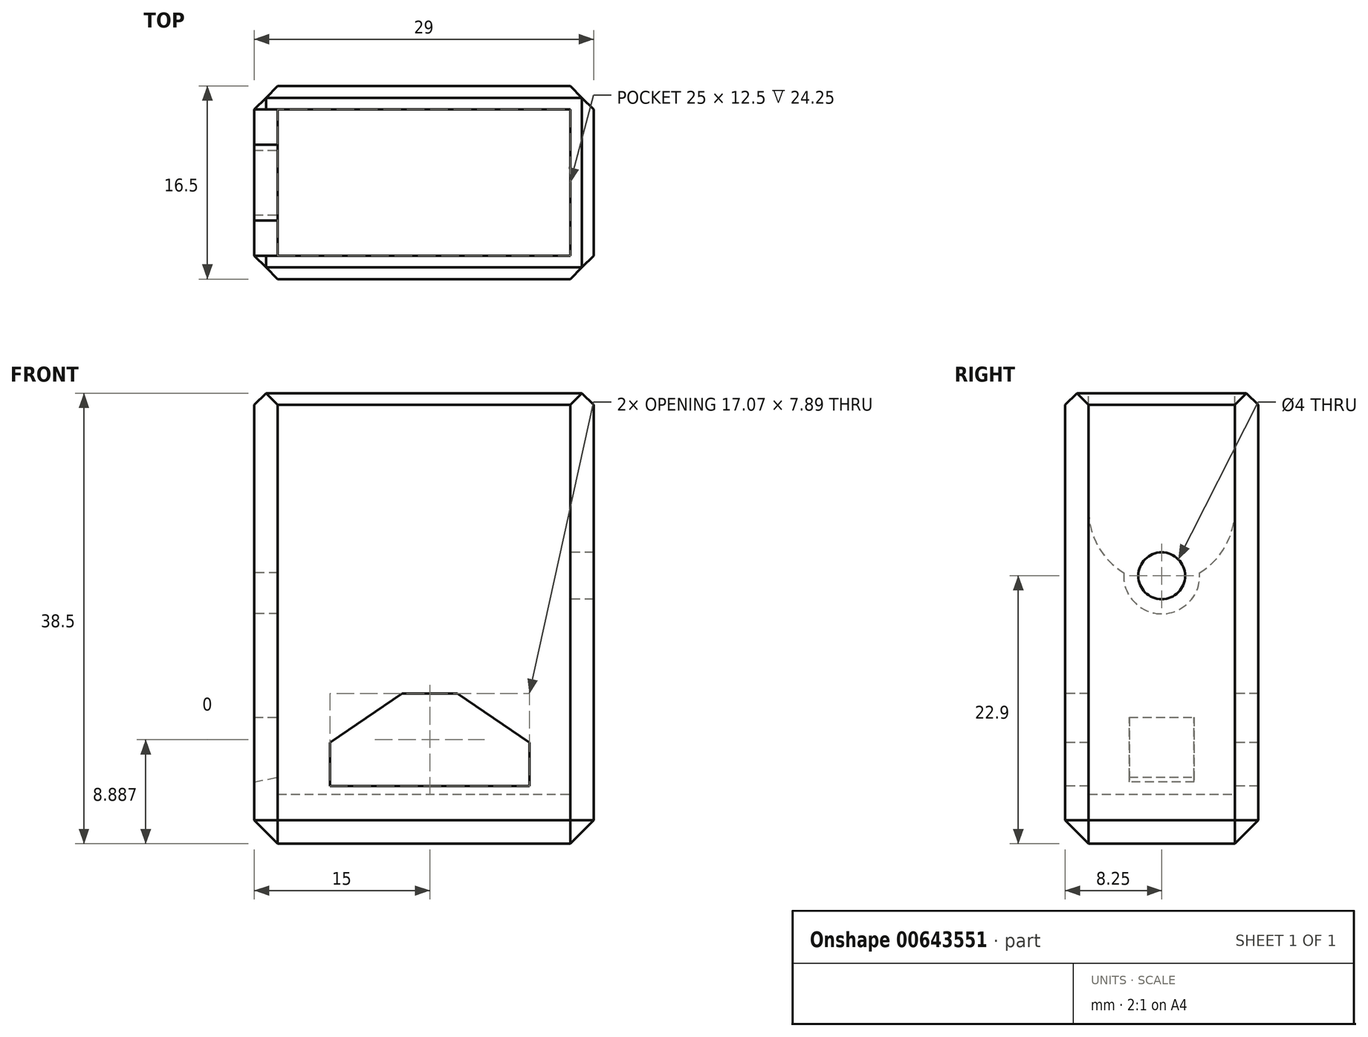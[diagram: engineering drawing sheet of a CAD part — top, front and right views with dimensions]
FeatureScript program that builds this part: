
annotation { "Feature Type Name" : "Feature", "Feature Type Description" : "" }
export const myFeature = defineFeature(function(context is Context, id is Id, definition is map)
    precondition{}
    {
        {
            var Q0;
            Q0=qCreatedBy(makeId("Top.planeOp"),FACE);
            var sketch = newSketch(context, id + "F0", { "sketchPlane" : qUnion([Q0])});
            skLineSegment(sketch, "E0.bottom", {"start": v(0, 0) * mm, "end": v(29, 0) * mm});
            skLineSegment(sketch, "E0.top", {"start": v(0, 16.5) * mm, "end": v(29, 16.5) * mm});
            skLineSegment(sketch, "E0.left", {"start": v(0, 0) * mm, "end": v(0, 16.5) * mm});
            skLineSegment(sketch, "E0.right", {"start": v(29, 0) * mm, "end": v(29, 16.5) * mm});
            skSolve(sketch);
        }
        {
            var Q0;
            Q0 = qSketchRegion(id + "F0", true);
            extrude(context, id + "F1", {"entities" : qUnion([Q0]), "depth" : 38.5 * mm, "offsetDistance" : 25 * mm});
        }
        {
            var Q0;
            Q0=makeQuery(id+"F1.opExtrude","CAP_FACE",FACE,{"disambiguationData":[OSD([sQuery(id+"F0.wireOp",EDGE,"E0.bottom"),sQuery(id+"F0.wireOp",EDGE,"E0.top"),sQuery(id+"F0.wireOp",EDGE,"E0.left"),sQuery(id+"F0.wireOp",EDGE,"E0.right")])],"isStart":false});
            shell(context, id + "F2", {"entities" : qUnion([Q0]), "thickness" : 2 * mm});
        }
        {
            var Q0;
            Q0=makeQuery(id+"F2.opShell","OFFSET_FACE",FACE,{"disambiguationData":[OSD([sQuery(id+"F0.wireOp",EDGE,"E0.bottom"),sQuery(id+"F0.wireOp",EDGE,"E0.top"),sQuery(id+"F0.wireOp",EDGE,"E0.left"),sQuery(id+"F0.wireOp",EDGE,"E0.right")])]});
            extrude(context, id + "F3", {"entities" : qUnion([Q0]), "operationType" : NewBodyOperationType.ADD, "depth" : 2.25 * mm, "offsetDistance" : 25 * mm});
        }
        {
            var Q0;
            Q0=makeQuery(id+"F1.opExtrude","SWEPT_EDGE",EDGE,{"disambiguationData":[OSD([sQuery(id+"F0.wireOp",EDGE,"E0.bottom"),sQuery(id+"F0.wireOp",EDGE,"E0.right")])]});
            var Q1;
            Q1=makeQuery(id+"F1.opExtrude","SWEPT_EDGE",EDGE,{"disambiguationData":[OSD([sQuery(id+"F0.wireOp",EDGE,"E0.top"),sQuery(id+"F0.wireOp",EDGE,"E0.right")])]});
            var Q2;
            Q2=makeQuery(id+"F1.opExtrude","SWEPT_EDGE",EDGE,{"disambiguationData":[OSD([sQuery(id+"F0.wireOp",EDGE,"E0.bottom"),sQuery(id+"F0.wireOp",EDGE,"E0.left")])]});
            var Q3;
            Q3=makeQuery(id+"F1.opExtrude","SWEPT_EDGE",EDGE,{"disambiguationData":[OSD([sQuery(id+"F0.wireOp",EDGE,"E0.top"),sQuery(id+"F0.wireOp",EDGE,"E0.left")])]});
            var Q4;
            Q4=makeQuery(id+"F1.opExtrude","CAP_EDGE",EDGE,{"disambiguationData":[OSD([sQuery(id+"F0.wireOp",EDGE,"E0.bottom")])],"isStart":true});
            var Q5;
            Q5=makeQuery(id+"F1.opExtrude","CAP_EDGE",EDGE,{"disambiguationData":[OSD([sQuery(id+"F0.wireOp",EDGE,"E0.left")])],"isStart":true});
            var Q6;
            Q6=makeQuery(id+"F1.opExtrude","CAP_EDGE",EDGE,{"disambiguationData":[OSD([sQuery(id+"F0.wireOp",EDGE,"E0.top")])],"isStart":true});
            var Q7;
            Q7=makeQuery(id+"F1.opExtrude","CAP_EDGE",EDGE,{"disambiguationData":[OSD([sQuery(id+"F0.wireOp",EDGE,"E0.right")])],"isStart":true});
            chamfer(context, id + "F4", {"entities" : qUnion([Q0, Q1, Q2, Q3, Q4, Q5, Q6, Q7]), "width" : 2 * mm, "tangentPropagation" : true});
        }
        {
            var Q0;
            Q0=makeQuery(id+"F1.opExtrude","CAP_EDGE",EDGE,{"disambiguationData":[OSD([sQuery(id+"F0.wireOp",EDGE,"E0.bottom")])],"isStart":false});
            var Q1;
            Q1=makeQuery(id+"F1.opExtrude","CAP_EDGE",EDGE,{"disambiguationData":[OSD([sQuery(id+"F0.wireOp",EDGE,"E0.right")])],"isStart":false});
            var Q2;
            Q2=makeQuery(id+"F1.opExtrude","CAP_EDGE",EDGE,{"disambiguationData":[OSD([sQuery(id+"F0.wireOp",EDGE,"E0.top")])],"isStart":false});
            var Q3;
            Q3=makeQuery(id+"F1.opExtrude","CAP_EDGE",EDGE,{"disambiguationData":[OSD([sQuery(id+"F0.wireOp",EDGE,"E0.left")])],"isStart":false});
            chamfer(context, id + "F5", {"entities" : qUnion([Q0, Q1, Q2, Q3]), "width" : 1 * mm, "tangentPropagation" : true});
        }
        {
            var Q0;
            Q0=makeQuery(id+"F1.opExtrude","SWEPT_FACE",FACE,{"disambiguationData":[OSD([sQuery(id+"F0.wireOp",EDGE,"E0.bottom")])]});
            var sketch = newSketch(context, id + "F6", { "sketchPlane" : qUnion([Q0])});
            skLineSegment(sketch, "E1", {"start": v(6.46, 4.94) * mm, "end": v(23.54, 4.94) * mm});
            skLineSegment(sketch, "E2", {"start": v(23.54, 4.94) * mm, "end": v(23.54, 8.66) * mm});
            skLineSegment(sketch, "E3", {"start": v(23.54, 8.66) * mm, "end": v(17.36, 12.83) * mm});
            skLineSegment(sketch, "E4", {"start": v(17.36, 12.83) * mm, "end": v(12.63, 12.83) * mm});
            skLineSegment(sketch, "E5", {"start": v(12.63, 12.83) * mm, "end": v(6.46, 8.66) * mm});
            skLineSegment(sketch, "E6", {"start": v(6.46, 8.66) * mm, "end": v(6.46, 4.94) * mm});
            skSolve(sketch);
        }
        {
            var Q0;
            Q0 = qSketchRegion(id + "F6", true);
            extrude(context, id + "F7", {"entities" : qUnion([Q0]), "operationType" : NewBodyOperationType.REMOVE, "endBound" : BoundingType.THROUGH_ALL, "oppositeDirection" : true, "depth" : 25 * mm, "offsetDistance" : 25 * mm});
        }
        {
            var Q0;
            Q0=qCreatedBy(makeId("Right.planeOp"),FACE);
            var sketch = newSketch(context, id + "F8", { "sketchPlane" : qUnion([Q0])});
            skLineSegment(sketch, "E7.bottom", {"start": v(2, 38.5) * mm, "end": v(14.5, 38.5) * mm});
            skLineSegment(sketch, "E7.top", {"start": v(2, 28.5) * mm, "end": v(14.5, 28.5) * mm});
            skLineSegment(sketch, "E7.left", {"start": v(2, 38.5) * mm, "end": v(2, 28.5) * mm});
            skLineSegment(sketch, "E7.right", {"start": v(14.5, 38.5) * mm, "end": v(14.5, 28.5) * mm});
            skCircle(sketch, "E8", {"center": v(8.25, 28.5) * mm, "radius": 6.25 * mm});
            skPoint(sketch, "E8.centerSnap0", {"position": v(8.25, 28.5) * mm});
            skCircle(sketch, "E9", {"center": v(8.25, 22.9) * mm, "radius": 3.25 * mm});
            skSolve(sketch);
        }
        {
            var Q0;
            Q0 = qSketchRegion(id + "F8", true);
            extrude(context, id + "F9", {"entities" : qUnion([Q0]), "operationType" : NewBodyOperationType.REMOVE, "endBound" : BoundingType.UP_TO_NEXT, "depth" : 25 * mm, "offsetDistance" : 25 * mm});
        }
        {
            var Q0;
            Q0=makeQuery(id+"F2.opShell","OFFSET_FACE",FACE,{"disambiguationData":[OSD([sQuery(id+"F0.wireOp",EDGE,"E0.right")])]});
            var sketch = newSketch(context, id + "F10", { "sketchPlane" : qUnion([Q0])});
            skCircle(sketch, "E10", {"center": v(-8.25, 22.9) * mm, "radius": 2 * mm});
            skSolve(sketch);
        }
        {
            var Q0;
            Q0=makeQuery(id+"F10.imprint","IMPRINT",FACE,{"disambiguationData":[TD([[makeQuery(id+"F10.imprint","IMPRINT",EDGE,{"derivedFrom":sQuery(id+"F10.wireOp",EDGE,"E10")}),1.0]])]});
            extrude(context, id + "F11", {"entities" : qUnion([Q0]), "operationType" : NewBodyOperationType.REMOVE, "endBound" : BoundingType.THROUGH_ALL, "oppositeDirection" : true, "depth" : 25 * mm, "offsetDistance" : 25 * mm});
        }
        {
            var Q0;
            Q0=makeQuery(id+"F1.opExtrude","SWEPT_FACE",FACE,{"disambiguationData":[OSD([sQuery(id+"F0.wireOp",EDGE,"E0.left")])]});
            var sketch = newSketch(context, id + "F12", { "sketchPlane" : qUnion([Q0])});
            skLineSegment(sketch, "E11.bottom", {"start": v(-11.02, 10.8) * mm, "end": v(-5.48, 10.8) * mm});
            skLineSegment(sketch, "E11.top", {"start": v(-11.02, 5.27) * mm, "end": v(-5.48, 5.27) * mm});
            skLineSegment(sketch, "E11.left", {"start": v(-11.02, 10.8) * mm, "end": v(-11.02, 5.27) * mm});
            skLineSegment(sketch, "E11.right", {"start": v(-5.48, 10.8) * mm, "end": v(-5.48, 5.27) * mm});
            skSolve(sketch);
        }
        {
            var Q0;
            Q0=makeQuery(id+"F12.imprint","IMPRINT",FACE,{"disambiguationData":[TD([[makeQuery(id+"F12.imprint","IMPRINT",EDGE,{"derivedFrom":sQuery(id+"F12.wireOp",EDGE,"E11.bottom")}),1.0]])]});
            cPlane(context, id + "F13", {"entities" : qUnion([Q0]), "cplaneType" : CPlaneType.OFFSET, "offset" : 4.45 * mm, "oppositeDirection" : true, "width" : 150 * mm, "height" : 150 * mm});
        }
        {
            var Q0;
            Q0=qCreatedBy(id+"F13.planeOp",FACE);
            var sketch = newSketch(context, id + "F14", { "sketchPlane" : qUnion([Q0])});
            skLineSegment(sketch, "E12.bottom", {"start": v(-11.02, 10.8) * mm, "end": v(-5.48, 10.8) * mm});
            skLineSegment(sketch, "E12.top", {"start": v(-11.02, 6.22) * mm, "end": v(-5.48, 6.22) * mm});
            skLineSegment(sketch, "E12.left", {"start": v(-11.02, 10.8) * mm, "end": v(-11.02, 6.22) * mm});
            skLineSegment(sketch, "E12.right", {"start": v(-5.48, 10.8) * mm, "end": v(-5.48, 6.22) * mm});
            skSolve(sketch);
        }
        {
            var Q1;
            Q1=makeQuery(id+"F12.imprint","IMPRINT",FACE,{"disambiguationData":[TD([[makeQuery(id+"F12.imprint","IMPRINT",EDGE,{"derivedFrom":sQuery(id+"F12.wireOp",EDGE,"E11.bottom")}),-1.0]])]});
            var Q2;
            Q2=makeQuery(id+"F14.imprint","IMPRINT",FACE,{"disambiguationData":[TD([[makeQuery(id+"F14.imprint","IMPRINT",EDGE,{"derivedFrom":sQuery(id+"F14.wireOp",EDGE,"E12.bottom")}),-1.0]])]});
            loft(context, id + "F15", {"operationType" : NewBodyOperationType.REMOVE, "sheetProfilesArray" : [{ "sheetProfileEntities" : qUnion([Q1]) }, { "sheetProfileEntities" : qUnion([Q2]) }]});
        }
    });
